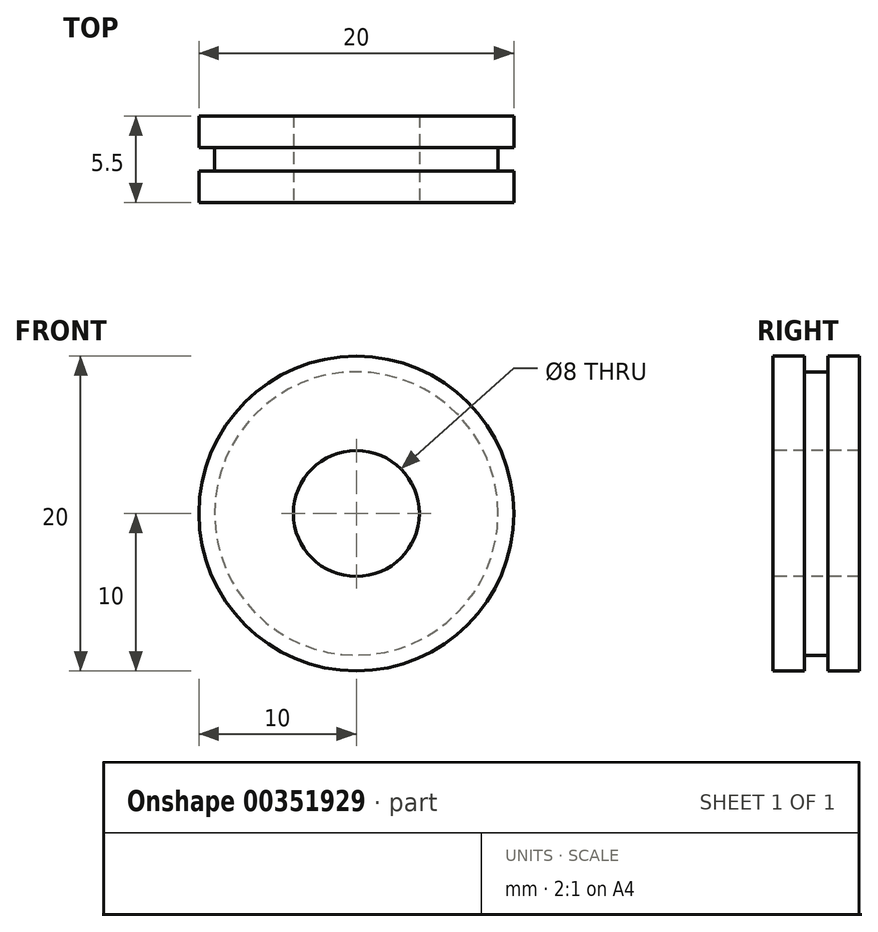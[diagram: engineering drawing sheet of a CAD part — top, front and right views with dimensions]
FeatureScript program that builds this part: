
annotation { "Feature Type Name" : "Feature", "Feature Type Description" : "" }
export const myFeature = defineFeature(function(context is Context, id is Id, definition is map)
    precondition{}
    {
        {
            var Q0;
            Q0=qCreatedBy(makeId("Front.planeOp"),FACE);
            var sketch = newSketch(context, id + "F0", { "sketchPlane" : qUnion([Q0])});
            skCircle(sketch, "E0", {"center": v(0, 0) * mm, "radius": 9 * mm});
            skSolve(sketch);
        }
        {
            var Q0;
            Q0 = qSketchRegion(id + "F0", true);
            extrude(context, id + "F1", {"entities" : qUnion([Q0]), "depth" : 1.5 * mm});
        }
        {
            var Q0;
            Q0=makeQuery(id+"F1.opExtrude","CAP_FACE",FACE,{"disambiguationData":[OSD([sQuery(id+"F0.wireOp",EDGE,"E0")])],"isStart":false});
            var sketch = newSketch(context, id + "F2", { "sketchPlane" : qUnion([Q0])});
            skCircle(sketch, "E1", {"center": v(0, 0) * mm, "radius": 10 * mm});
            skSolve(sketch);
        }
        {
            var Q0;
            Q0 = qSketchRegion(id + "F2", true);
            extrude(context, id + "F3", {"entities" : qUnion([Q0]), "operationType" : NewBodyOperationType.ADD, "depth" : 2 * mm});
        }
        {
            var Q0;
            Q0=makeQuery(id+"F1.opExtrude","CAP_FACE",FACE,{"disambiguationData":[OSD([sQuery(id+"F0.wireOp",EDGE,"E0")])],"isStart":true});
            var sketch = newSketch(context, id + "F4", { "sketchPlane" : qUnion([Q0])});
            skCircle(sketch, "E2", {"center": v(0, 0) * mm, "radius": 10 * mm});
            skSolve(sketch);
        }
        {
            var Q0;
            Q0 = qSketchRegion(id + "F4", true);
            extrude(context, id + "F5", {"entities" : qUnion([Q0]), "operationType" : NewBodyOperationType.ADD, "depth" : 2 * mm});
        }
        {
            var Q0;
            Q0=makeQuery(id+"F3.opExtrude","CAP_FACE",FACE,{"disambiguationData":[OSD([sQuery(id+"F2.wireOp",EDGE,"E1")])],"isStart":false});
            var sketch = newSketch(context, id + "F6", { "sketchPlane" : qUnion([Q0])});
            skPoint(sketch, "E3", {"position": v(0, 0) * mm});
            skSolve(sketch);
        }
        {
            var Q0;
            Q0=sQuery(id+"F6.wireOp",VERTEX,"E3");
            var Q1;
            Q1=makeQuery(id+"F1.opExtrude","SWEPT_BODY",BODY,{"disambiguationData":[OSD([sQuery(id+"F0.wireOp",EDGE,"E0")])]});
            hole(context, id + "F7", {"style" : HoleStyle.SIMPLE, "endStyle" : HoleEndStyle.THROUGH, "holeDiameter" : 8 * mm, "isTappedThrough" : true, "tappedDepth" : 12 * mm, "tapClearance" : 3, "locations" : qUnion([Q0]), "scope" : qUnion([Q1])});
        }
    });
